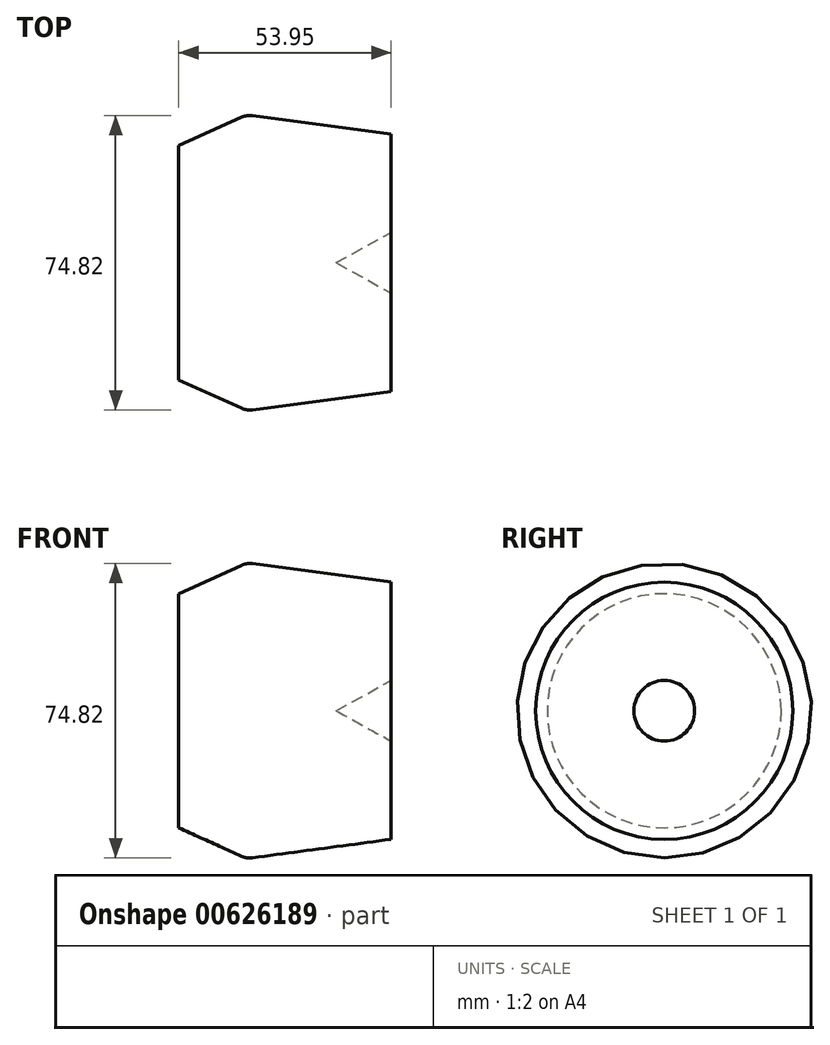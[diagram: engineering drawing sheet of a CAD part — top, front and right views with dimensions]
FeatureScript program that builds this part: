
annotation { "Feature Type Name" : "Feature", "Feature Type Description" : "" }
export const myFeature = defineFeature(function(context is Context, id is Id, definition is map)
    precondition{}
    {
        {
            var Q0;
            Q0=qCreatedBy(makeId("Front.planeOp"),FACE);
            var sketch = newSketch(context, id + "F0", { "sketchPlane" : qUnion([Q0])});
            skLineSegment(sketch, "E0", {"start": v(0, 0) * mm, "end": v(0, 29.73) * mm});
            skLineSegment(sketch, "E1", {"start": v(0, 29.73) * mm, "end": v(17.25, 37.56) * mm});
            skLineSegment(sketch, "E2", {"start": v(17.25, 37.56) * mm, "end": v(53.95, 32.66) * mm});
            skLineSegment(sketch, "E3", {"start": v(53.95, 32.66) * mm, "end": v(53.95, 7.7) * mm});
            skLineSegment(sketch, "E4", {"start": v(53.95, 7.7) * mm, "end": v(40, 0) * mm});
            skLineSegment(sketch, "E5", {"start": v(40, 0) * mm, "end": v(0, 0) * mm});
            skLineSegment(sketch, "E6", {"start": v(0, 0) * mm, "end": v(-41.47, 0) * mm, "construction": true});
            skSolve(sketch);
        }
        {
            var Q0;
            Q0 = qSketchRegion(id + "F0", true);
            var Q1;
            Q1=sQuery(id+"F0.wireOp",EDGE,"E6");
            revolve(context, id + "F1", {"entities" : qUnion([Q0]), "axis" : qUnion([Q1]), "revolveType" : RevolveType.FULL});
        }
        {
            var Q0;
            Q0=makeQuery(id+"F1.opRevolve","SWEPT_EDGE",EDGE,{"disambiguationData":[OSD([sQuery(id+"F0.wireOp",EDGE,"E1"),sQuery(id+"F0.wireOp",EDGE,"E2")])]});
            fillet(context, id + "F2", {"entities" : qUnion([Q0]), "radius" : 5.08 * mm, "tangentPropagation" : true, "allowEdgeOverflow" : false});
        }
    });
